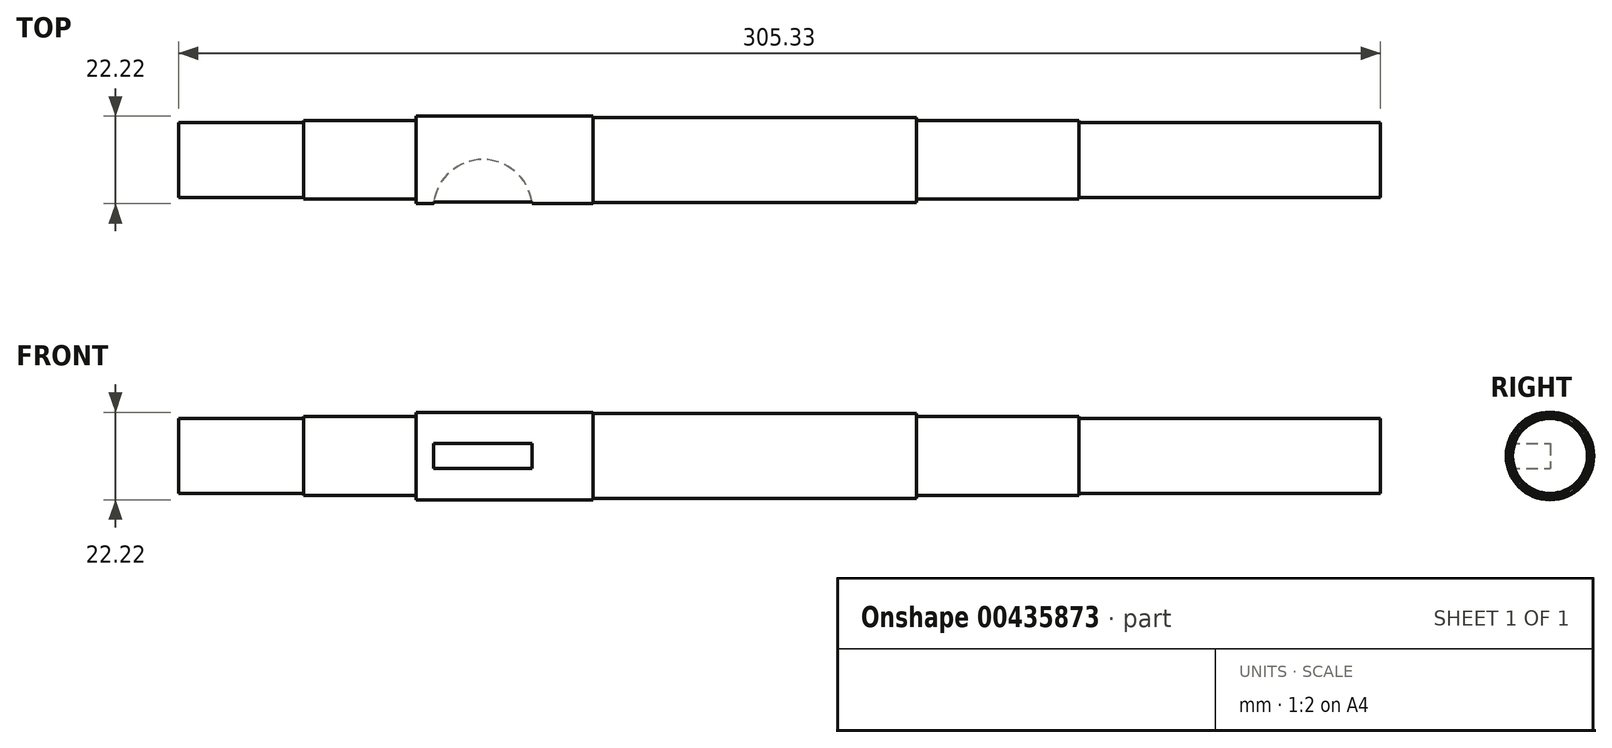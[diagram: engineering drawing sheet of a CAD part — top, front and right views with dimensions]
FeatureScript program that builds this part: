
annotation { "Feature Type Name" : "Feature", "Feature Type Description" : "" }
export const myFeature = defineFeature(function(context is Context, id is Id, definition is map)
    precondition{}
    {
        {
            var Q0;
            Q0=qCreatedBy(makeId("Right.planeOp"),FACE);
            var sketch = newSketch(context, id + "F0", { "sketchPlane" : qUnion([Q0])});
            skCircle(sketch, "E0", {"center": v(0, 0) * mm, "radius": 9.53 * mm});
            skSolve(sketch);
        }
        {
            var Q0;
            Q0 = qSketchRegion(id + "F0", true);
            extrude(context, id + "F1", {"entities" : qUnion([Q0]), "depth" : 31.75 * mm});
        }
        {
            var Q0;
            Q0=makeQuery(id+"F1.opExtrude","CAP_FACE",FACE,{"disambiguationData":[OSD([sQuery(id+"F0.wireOp",EDGE,"E0")])],"isStart":false});
            var sketch = newSketch(context, id + "F2", { "sketchPlane" : qUnion([Q0])});
            skCircle(sketch, "E1", {"center": v(0, 0) * mm, "radius": 10 * mm});
            skSolve(sketch);
        }
        {
            var Q0;
            Q0 = qSketchRegion(id + "F2", true);
            extrude(context, id + "F3", {"entities" : qUnion([Q0]), "operationType" : NewBodyOperationType.ADD, "depth" : 28.57 * mm});
        }
        {
            var Q0;
            Q0=makeQuery(id+"F3.opExtrude","CAP_FACE",FACE,{"disambiguationData":[OSD([sQuery(id+"F2.wireOp",EDGE,"E1")])],"isStart":false});
            var sketch = newSketch(context, id + "F4", { "sketchPlane" : qUnion([Q0])});
            skCircle(sketch, "E2", {"center": v(0, 0) * mm, "radius": 11.11 * mm});
            skSolve(sketch);
        }
        {
            var Q0;
            Q0 = qSketchRegion(id + "F4", true);
            extrude(context, id + "F5", {"entities" : qUnion([Q0]), "operationType" : NewBodyOperationType.ADD, "depth" : 45.03 * mm});
        }
        {
            var Q0;
            Q0=makeQuery(id+"F5.opExtrude","CAP_FACE",FACE,{"disambiguationData":[OSD([sQuery(id+"F4.wireOp",EDGE,"E2")])],"isStart":false});
            var sketch = newSketch(context, id + "F6", { "sketchPlane" : qUnion([Q0])});
            skCircle(sketch, "E3", {"center": v(0, 0) * mm, "radius": 10.77 * mm});
            skSolve(sketch);
        }
        {
            var Q0;
            Q0 = qSketchRegion(id + "F6", true);
            extrude(context, id + "F7", {"entities" : qUnion([Q0]), "operationType" : NewBodyOperationType.ADD, "depth" : 82.17 * mm});
        }
        {
            var Q0;
            Q0=makeQuery(id+"F7.opExtrude","CAP_FACE",FACE,{"disambiguationData":[OSD([sQuery(id+"F6.wireOp",EDGE,"E3")])],"isStart":false});
            var sketch = newSketch(context, id + "F8", { "sketchPlane" : qUnion([Q0])});
            skCircle(sketch, "E4", {"center": v(0, 0) * mm, "radius": 10 * mm});
            skSolve(sketch);
        }
        {
            var Q0;
            Q0 = qSketchRegion(id + "F8", true);
            extrude(context, id + "F9", {"entities" : qUnion([Q0]), "operationType" : NewBodyOperationType.ADD, "depth" : 41.27 * mm});
        }
        {
            var Q0;
            Q0=makeQuery(id+"F9.opExtrude","CAP_FACE",FACE,{"disambiguationData":[OSD([sQuery(id+"F8.wireOp",EDGE,"E4")])],"isStart":false});
            var sketch = newSketch(context, id + "F10", { "sketchPlane" : qUnion([Q0])});
            skCircle(sketch, "E5", {"center": v(0, 0) * mm, "radius": 9.53 * mm});
            skSolve(sketch);
        }
        {
            var Q0;
            Q0 = qSketchRegion(id + "F10", true);
            extrude(context, id + "F11", {"entities" : qUnion([Q0]), "operationType" : NewBodyOperationType.ADD, "depth" : 76.53 * mm});
        }
        {
            var Q0;
            Q0=qCreatedBy(makeId("Top.planeOp"),FACE);
            var sketch = newSketch(context, id + "F12", { "sketchPlane" : qUnion([Q0])});
            skCircle(sketch, "E6", {"center": v(77.32, -12.48) * mm, "radius": 12.59 * mm});
            skSolve(sketch);
        }
        {
            var Q0;
            Q0=makeQuery(id+"F12.imprint","IMPRINT",FACE,{"disambiguationData":[TD([[makeQuery(id+"F12.imprint","IMPRINT",EDGE,{"derivedFrom":sQuery(id+"F12.wireOp",EDGE,"E6")}),1.0]])]});
            extrude(context, id + "F13", {"entities" : qUnion([Q0]), "operationType" : NewBodyOperationType.REMOVE, "depth" : 3.17 * mm});
        }
        {
            var Q0;
            Q0=makeQuery(id+"F13.boolean.opBoolean","COPY",FACE,{"derivedFrom":makeQuery(id+"F13.opExtrude","CAP_FACE",FACE,{"disambiguationData":[OSD([sQuery(id+"F12.wireOp",EDGE,"E6")])],"isStart":true})});
            extrude(context, id + "F14", {"entities" : qUnion([Q0]), "operationType" : NewBodyOperationType.REMOVE, "oppositeDirection" : true, "depth" : 3.17 * mm});
        }
    });
